# Revit family: Domotics-DomesticRanges-GEWISS-27COMBI_SYSTEM-IP55_FLASHLIGHTS
name_source: partatom
category: Apparecchi elettrici
revit_build: Autodesk Revit 2016 (Build: 20161004_0715(x64)
units: mm (PartAtom-declared; Revit-internal decimal feet)

## family parameters
Condiviso = No
Host = Muro
Mantenere orientamento annotazione = No
Numero OmniClass = 23.80.50.00
Punto di calcolo locali = No
Quota connettore circolare = Usa diametro
Sempre verticale = Sì
Taglio con vuoti quando caricato = No
Tipo di parte = Normale
Titolo OmniClass = Terminals for Power Supply

## types (4) — shared parameters
Catalogue = DOMOTICS
Catalogue Range = 27COMBI
Colore diffusore = GEWISS VETRINO GIALLO
Colour = Grey RAL 7035
Electrocod = 0132
Flash frequency = 1HZ
Glow Wire Test = 650°C
IDF = ec85d665-b2b6-4258-8af3-fa800f1490ef
IDT = 642694f6-aaf2-4b3c-9aa4-08d332f019c7
IP degree = IP55
Immagine tipo = GW27424.jpg
Installation temperature = -25 +60 °C
Insulation class = II
Lampholder type = E14
NUMERO DI POLI = 1
Outer dim. LxHxD (mm) = 66x82x95
Power = Max 25W
Produttore = GEWISS S.p.A.
Standard = EN 60598-1
Technical sheet = https://www.gewiss.com
Thermo-pressure with ball = 70
URL = https://www.gewiss.com
Version file RFA = 18.0

## per-type parameters (varying)
| type | Descrizione | Diffuser colour | EAN code | Modello | Rated voltage |
| GW27424 - 230V yellow electr.flashlight | 230V YELLOW ELECTR.FLASHLIGHT | Yellow | 8011564056251 | GW27424 | 230V ac |
| GW27423 - 24V yellow electr.flashlight | 24V YELLOW ELECTR.FLASHLIGHT | Yellow | 8011564056244 | GW27423 | 24 V ac |
| GW27421 - 24V red electr.flashlight | 24V RED ELECTR.FLASHLIGHT | Red | 8011564056220 | GW27421 | 24 V ac |
| GW27422 - 230V red electronic flashlight | 230V RED ELECTRONIC FLASHLIGHT | Red | 8011564056237 | GW27422 | 230V ac |

note: source unit labels omitted for Thermo-pressure with ball — the stored unit's dimension contradicts the parameter name (converter mislabeling)
